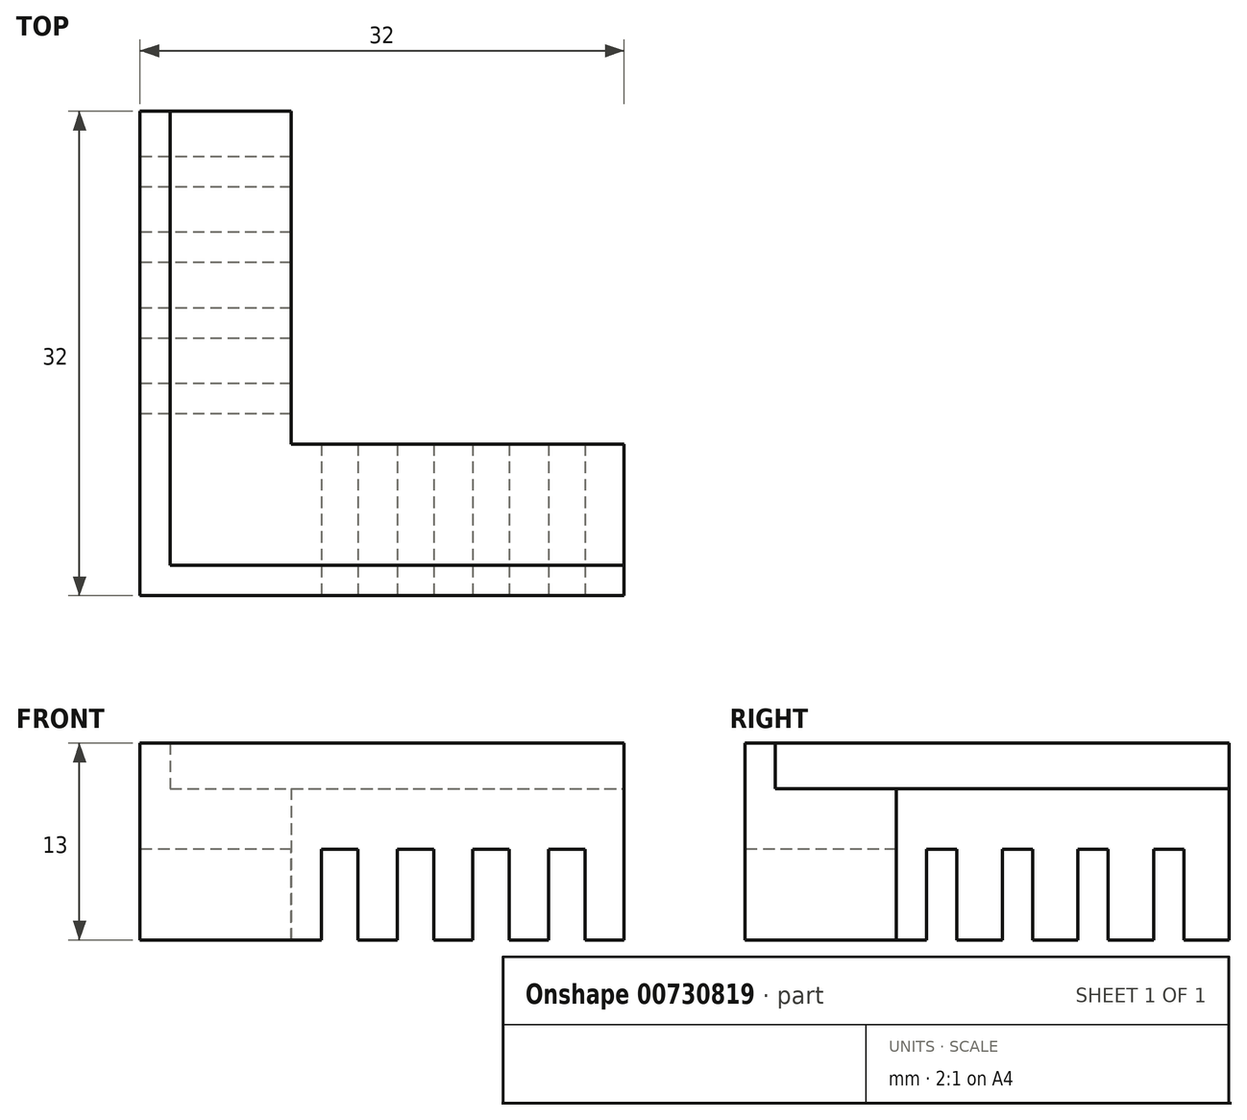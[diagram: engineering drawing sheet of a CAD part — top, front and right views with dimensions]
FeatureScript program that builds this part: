
annotation { "Feature Type Name" : "Feature", "Feature Type Description" : "" }
export const myFeature = defineFeature(function(context is Context, id is Id, definition is map)
    precondition{}
    {
        {
            var Q0;
            Q0=qCreatedBy(makeId("Top.planeOp"),FACE);
            var sketch = newSketch(context, id + "F0", { "sketchPlane" : qUnion([Q0])});
            skLineSegment(sketch, "E0.bottom", {"start": v(0, 0) * mm, "end": v(8, 0) * mm});
            skLineSegment(sketch, "E0.top", {"start": v(0, 22) * mm, "end": v(8, 22) * mm});
            skLineSegment(sketch, "E0.left", {"start": v(0, 0) * mm, "end": v(0, 22) * mm});
            skLineSegment(sketch, "E0.right", {"start": v(8, 0) * mm, "end": v(8, 22) * mm});
            skLineSegment(sketch, "E1.bottom", {"start": v(8, 0) * mm, "end": v(30, 0) * mm});
            skLineSegment(sketch, "E1.top", {"start": v(0, -8) * mm, "end": v(30, -8) * mm});
            skLineSegment(sketch, "E1.left", {"start": v(0, 0) * mm, "end": v(0, -8) * mm});
            skLineSegment(sketch, "E1.right", {"start": v(30, 0) * mm, "end": v(30, -8) * mm});
            skLineSegment(sketch, "E2.0", {"start": v(-2, 11.9) * mm, "end": v(-2, 22) * mm});
            skLineSegment(sketch, "E2.1", {"start": v(-2, 11.9) * mm, "end": v(-2, -10) * mm});
            skLineSegment(sketch, "E2.2", {"start": v(-2, -10) * mm, "end": v(30, -10) * mm});
            skLineSegment(sketch, "E3", {"start": v(-2, 22) * mm, "end": v(0, 22) * mm});
            skLineSegment(sketch, "E4", {"start": v(30, -8) * mm, "end": v(30, -10) * mm});
            skSolve(sketch);
        }
        {
            var Q0;
            Q0=makeQuery(id+"F0.imprint","IMPRINT",FACE,{"disambiguationData":[TD([[makeQuery(id+"F0.imprint","IMPRINT",EDGE,{"derivedFrom":sQuery(id+"F0.wireOp",EDGE,"E0.left")}),1.0]])]});
            extrude(context, id + "F1", {"entities" : qUnion([Q0]), "depth" : 13 * mm, "offsetDistance" : 25 * mm});
        }
        {
            var Q0;
            Q0=makeQuery(id+"F0.imprint","IMPRINT",FACE,{"disambiguationData":[TD([[makeQuery(id+"F0.imprint","IMPRINT",EDGE,{"derivedFrom":sQuery(id+"F0.wireOp",EDGE,"E0.bottom")}),1.0]])]});
            var Q1;
            Q1=makeQuery(id+"F0.imprint","IMPRINT",FACE,{"disambiguationData":[TD([[makeQuery(id+"F0.imprint","IMPRINT",EDGE,{"derivedFrom":sQuery(id+"F0.wireOp",EDGE,"E0.bottom")}),-1.0]])]});
            extrude(context, id + "F2", {"entities" : qUnion([Q0, Q1]), "operationType" : NewBodyOperationType.ADD, "depth" : 10 * mm, "offsetDistance" : 25 * mm});
        }
        {
            var Q0;
            Q0=makeQuery(id+"F1.opExtrude","SWEPT_FACE",FACE,{"disambiguationData":[OSD([sQuery(id+"F0.wireOp",EDGE,"E2.2")])]});
            var sketch = newSketch(context, id + "F3", { "sketchPlane" : qUnion([Q0])});
            skLineSegment(sketch, "E5.bottom", {"start": v(0, 0) * mm, "end": v(2.4, 0) * mm});
            skLineSegment(sketch, "E5.top", {"start": v(0, 6) * mm, "end": v(2.4, 6) * mm});
            skLineSegment(sketch, "E5.left", {"start": v(0, 0) * mm, "end": v(0, 6) * mm});
            skLineSegment(sketch, "E5.right", {"start": v(2.4, 0) * mm, "end": v(2.4, 6) * mm});
            skLineSegment(sketch, "E6.1.0.0", {"start": v(5, 0) * mm, "end": v(5, 6) * mm});
            skLineSegment(sketch, "E6.1.0.1", {"start": v(5, 6) * mm, "end": v(7.4, 6) * mm});
            skLineSegment(sketch, "E6.1.0.2", {"start": v(7.4, 0) * mm, "end": v(7.4, 6) * mm});
            skLineSegment(sketch, "E6.2.0.0", {"start": v(10, 0) * mm, "end": v(10, 6) * mm});
            skLineSegment(sketch, "E6.2.0.1", {"start": v(10, 6) * mm, "end": v(12.4, 6) * mm});
            skLineSegment(sketch, "E6.2.0.2", {"start": v(12.4, 0) * mm, "end": v(12.4, 6) * mm});
            skLineSegment(sketch, "E6.3.0.0", {"start": v(15, 0) * mm, "end": v(15, 6) * mm});
            skLineSegment(sketch, "E6.3.0.1", {"start": v(15, 6) * mm, "end": v(17.4, 6) * mm});
            skLineSegment(sketch, "E6.3.0.2", {"start": v(17.4, 0) * mm, "end": v(17.4, 6) * mm});
            skLineSegment(sketch, "E6.4.0.0", {"start": v(20, 0) * mm, "end": v(20, 6) * mm});
            skLineSegment(sketch, "E6.4.0.1", {"start": v(20, 6) * mm, "end": v(22.4, 6) * mm});
            skLineSegment(sketch, "E6.4.0.2", {"start": v(22.4, 0) * mm, "end": v(22.4, 6) * mm});
            skLineSegment(sketch, "E6.5.0.0", {"start": v(25, 0) * mm, "end": v(25, 6) * mm});
            skLineSegment(sketch, "E6.5.0.1", {"start": v(25, 6) * mm, "end": v(27.4, 6) * mm});
            skLineSegment(sketch, "E6.5.0.2", {"start": v(27.4, 0) * mm, "end": v(27.4, 6) * mm});
            skLineSegment(sketch, "E6.direction1", {"start": v(0, 0) * mm, "end": v(5, 0) * mm, "construction": true});
            skSolve(sketch);
        }
        {
            var Q0;
            Q0=makeQuery(id+"F1.opExtrude","SWEPT_FACE",FACE,{"disambiguationData":[OSD([sQuery(id+"F0.wireOp",EDGE,"E2.0"),sQuery(id+"F0.wireOp",EDGE,"E2.1")])]});
            var sketch = newSketch(context, id + "F4", { "sketchPlane" : qUnion([Q0])});
            skLineSegment(sketch, "E7.bottom", {"start": v(8, 0) * mm, "end": v(6, 0) * mm});
            skLineSegment(sketch, "E7.top", {"start": v(8, 6) * mm, "end": v(6, 6) * mm});
            skLineSegment(sketch, "E7.left", {"start": v(8, 0) * mm, "end": v(8, 6) * mm});
            skLineSegment(sketch, "E7.right", {"start": v(6, 0) * mm, "end": v(6, 6) * mm});
            skLineSegment(sketch, "E8.1.0.0", {"start": v(1, 0) * mm, "end": v(1, 6) * mm});
            skLineSegment(sketch, "E8.1.0.1", {"start": v(3, 6) * mm, "end": v(1, 6) * mm});
            skLineSegment(sketch, "E8.1.0.2", {"start": v(3, 0) * mm, "end": v(3, 6) * mm});
            skLineSegment(sketch, "E8.2.0.0", {"start": v(-4, 0) * mm, "end": v(-4, 6) * mm});
            skLineSegment(sketch, "E8.2.0.1", {"start": v(-2, 6) * mm, "end": v(-4, 6) * mm});
            skLineSegment(sketch, "E8.2.0.2", {"start": v(-2, 0) * mm, "end": v(-2, 6) * mm});
            skLineSegment(sketch, "E8.3.0.0", {"start": v(-9, 0) * mm, "end": v(-9, 6) * mm});
            skLineSegment(sketch, "E8.3.0.1", {"start": v(-7, 6) * mm, "end": v(-9, 6) * mm});
            skLineSegment(sketch, "E8.3.0.2", {"start": v(-7, 0) * mm, "end": v(-7, 6) * mm});
            skLineSegment(sketch, "E8.4.0.0", {"start": v(-14, 0) * mm, "end": v(-14, 6) * mm});
            skLineSegment(sketch, "E8.4.0.1", {"start": v(-12, 6) * mm, "end": v(-14, 6) * mm});
            skLineSegment(sketch, "E8.4.0.2", {"start": v(-12, 0) * mm, "end": v(-12, 6) * mm});
            skLineSegment(sketch, "E8.5.0.0", {"start": v(-19, 0) * mm, "end": v(-19, 6) * mm});
            skLineSegment(sketch, "E8.5.0.1", {"start": v(-17, 6) * mm, "end": v(-19, 6) * mm});
            skLineSegment(sketch, "E8.5.0.2", {"start": v(-17, 0) * mm, "end": v(-17, 6) * mm});
            skLineSegment(sketch, "E8.direction1", {"start": v(6, 0) * mm, "end": v(1, 0) * mm, "construction": true});
            skSolve(sketch);
        }
        {
            var Q0;
            {var subQ0=sQuery(id+"F3.wireOp",EDGE,"E6.2.0.0");Q0=makeQuery(id+"F3.imprint","IMPRINT",FACE,{"disambiguationData":[TD([[makeQuery(id+"F3.imprint","IMPRINT",EDGE,{"derivedFrom":subQ0}),-1.0]])]});}
            var Q1;
            {var subQ0=sQuery(id+"F3.wireOp",EDGE,"E6.3.0.0");Q1=makeQuery(id+"F3.imprint","IMPRINT",FACE,{"disambiguationData":[TD([[makeQuery(id+"F3.imprint","IMPRINT",EDGE,{"derivedFrom":subQ0}),-1.0]])]});}
            var Q2;
            {var subQ0=sQuery(id+"F3.wireOp",EDGE,"E6.4.0.0");Q2=makeQuery(id+"F3.imprint","IMPRINT",FACE,{"disambiguationData":[TD([[makeQuery(id+"F3.imprint","IMPRINT",EDGE,{"derivedFrom":subQ0}),-1.0]])]});}
            var Q3;
            {var subQ0=sQuery(id+"F3.wireOp",EDGE,"E6.5.0.0");Q3=makeQuery(id+"F3.imprint","IMPRINT",FACE,{"disambiguationData":[TD([[makeQuery(id+"F3.imprint","IMPRINT",EDGE,{"derivedFrom":subQ0}),-1.0]])]});}
            extrude(context, id + "F5", {"entities" : qUnion([Q0, Q1, Q2, Q3]), "operationType" : NewBodyOperationType.REMOVE, "oppositeDirection" : true, "depth" : 25 * mm, "offsetDistance" : 25 * mm});
        }
        {
            var Q0;
            {var subQ0=sQuery(id+"F4.wireOp",EDGE,"E8.4.0.0");Q0=makeQuery(id+"F4.imprint","IMPRINT",FACE,{"disambiguationData":[TD([[makeQuery(id+"F4.imprint","IMPRINT",EDGE,{"derivedFrom":subQ0}),-1.0]])]});}
            var Q1;
            {var subQ0=sQuery(id+"F4.wireOp",EDGE,"E8.5.0.0");Q1=makeQuery(id+"F4.imprint","IMPRINT",FACE,{"disambiguationData":[TD([[makeQuery(id+"F4.imprint","IMPRINT",EDGE,{"derivedFrom":subQ0}),-1.0]])]});}
            var Q2;
            {var subQ0=sQuery(id+"F4.wireOp",EDGE,"E8.3.0.0");Q2=makeQuery(id+"F4.imprint","IMPRINT",FACE,{"disambiguationData":[TD([[makeQuery(id+"F4.imprint","IMPRINT",EDGE,{"derivedFrom":subQ0}),-1.0]])]});}
            var Q3;
            {var subQ0=sQuery(id+"F4.wireOp",EDGE,"E8.2.0.0");Q3=makeQuery(id+"F4.imprint","IMPRINT",FACE,{"disambiguationData":[TD([[makeQuery(id+"F4.imprint","IMPRINT",EDGE,{"derivedFrom":subQ0}),-1.0]])]});}
            extrude(context, id + "F6", {"entities" : qUnion([Q0, Q1, Q2, Q3]), "operationType" : NewBodyOperationType.REMOVE, "oppositeDirection" : true, "depth" : 25 * mm, "offsetDistance" : 25 * mm});
        }
    });
